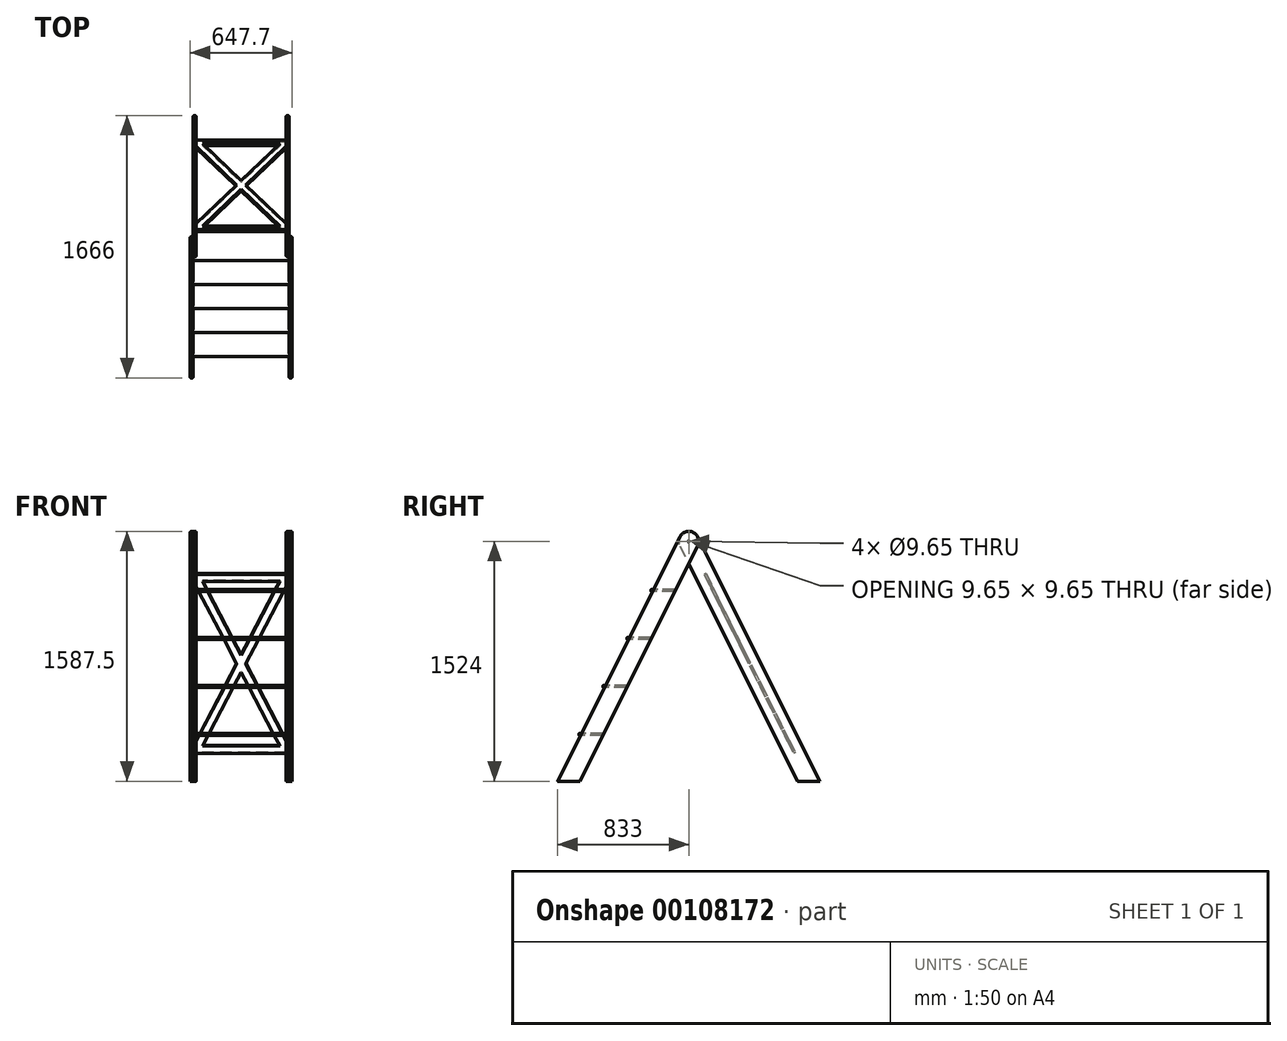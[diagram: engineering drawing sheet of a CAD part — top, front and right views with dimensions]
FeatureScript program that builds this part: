
annotation { "Feature Type Name" : "Feature", "Feature Type Description" : "" }
export const myFeature = defineFeature(function(context is Context, id is Id, definition is map)
    precondition{}
    {
        {
            var Q0;
            Q0=qCreatedBy(makeId("Right.planeOp"),FACE);
            var sketch = newSketch(context, id + "F0", { "sketchPlane" : qUnion([Q0])});
            skLineSegment(sketch, "E0", {"start": v(0, 0) * mm, "end": v(0, 1524) * mm, "construction": true});
            skLineSegment(sketch, "E1.0", {"start": v(-762, 0) * mm, "end": v(-762, 1524) * mm, "construction": true});
            skLineSegment(sketch, "E2", {"start": v(-691, 0) * mm, "end": v(-833, 0) * mm});
            skLineSegment(sketch, "E3.0", {"start": v(0, 304.8) * mm, "end": v(-1233.58, 304.8) * mm, "construction": true});
            skLineSegment(sketch, "E4.0", {"start": v(0, 609.6) * mm, "end": v(-1233.58, 609.6) * mm, "construction": true});
            skLineSegment(sketch, "E5.0", {"start": v(0, 914.4) * mm, "end": v(-1233.58, 914.4) * mm, "construction": true});
            skLineSegment(sketch, "E6.0", {"start": v(0, 1219.2) * mm, "end": v(-1233.58, 1219.2) * mm, "construction": true});
            skArc(sketch, "E7", {"start": v(-28.4, 1467.2) * mm, "mid": v(-14.59, 1462.2) * mm, "end": v(0, 1460.5) * mm, "construction": true});
            skLineSegment(sketch, "E8", {"start": v(0, 1524) * mm, "end": v(-762, 0) * mm, "construction": true});
            skLineSegment(sketch, "E9.0", {"start": v(-56.8, 1552.4) * mm, "end": v(-833, 0) * mm});
            skLineSegment(sketch, "E10.0", {"start": v(56.8, 1495.6) * mm, "end": v(-691, 0) * mm});
            skArc(sketch, "E11.trimOffspring", {"start": v(56.8, 1495.6) * mm, "mid": v(28.4, 1580.8) * mm, "end": v(-56.8, 1552.4) * mm});
            skSolve(sketch);
        }
        {
            var Q0;
            Q0=qSketchRegion(id+"F0",true);
            extrude(context, id + "F1", {"entities" : qUnion([Q0]), "depth" : 19.05 * mm});
        }
        {
            var Q0;
            Q0=makeQuery(id+"F1.opExtrude","CAP_FACE",FACE,{"disambiguationData":[OSD([sQuery(id+"F0.wireOp",EDGE,"E2"),sQuery(id+"F0.wireOp",EDGE,"E9.0"),sQuery(id+"F0.wireOp",EDGE,"E10.0"),sQuery(id+"F0.wireOp",EDGE,"E11.trimOffspring")])],"isStart":true});
            var sketch = newSketch(context, id + "F2", { "sketchPlane" : qUnion([Q0])});
            skLineSegment(sketch, "E12.0", {"start": v(56.8, 1552.4) * mm, "end": v(229.75, 1206.5) * mm});
            skLineSegment(sketch, "E13.0", {"start": v(-56.8, 1495.6) * mm, "end": v(87.75, 1206.5) * mm});
            skLineSegment(sketch, "E14.0", {"start": v(0, 1219.2) * mm, "end": v(1233.58, 1219.2) * mm});
            skLineSegment(sketch, "E15.0", {"start": v(0, 914.4) * mm, "end": v(1233.58, 914.4) * mm});
            skLineSegment(sketch, "E16.0", {"start": v(0, 609.6) * mm, "end": v(1233.58, 609.6) * mm});
            skLineSegment(sketch, "E17.0", {"start": v(0, 304.8) * mm, "end": v(1233.58, 304.8) * mm});
            skLineSegment(sketch, "E18.0", {"start": v(0, 1206.5) * mm, "end": v(1233.58, 1206.5) * mm});
            skLineSegment(sketch, "E19.0", {"start": v(0, 901.7) * mm, "end": v(1233.58, 901.7) * mm});
            skLineSegment(sketch, "E20.0", {"start": v(0, 596.9) * mm, "end": v(1233.58, 596.9) * mm});
            skLineSegment(sketch, "E21.0", {"start": v(0, 292.1) * mm, "end": v(1233.58, 292.1) * mm});
            skLineSegment(sketch, "E22.trimOffspring", {"start": v(375.8, 914.4) * mm, "end": v(382.15, 901.7) * mm});
            skLineSegment(sketch, "E23.trimOffspring", {"start": v(233.8, 914.4) * mm, "end": v(240.15, 901.7) * mm});
            skLineSegment(sketch, "E24.trimOffspring", {"start": v(528.2, 609.6) * mm, "end": v(534.55, 596.9) * mm});
            skLineSegment(sketch, "E25.trimOffspring", {"start": v(386.2, 609.6) * mm, "end": v(392.55, 596.9) * mm});
            skLineSegment(sketch, "E26.trimOffspring", {"start": v(680.6, 304.8) * mm, "end": v(686.95, 292.1) * mm});
            skLineSegment(sketch, "E27.trimOffspring", {"start": v(538.6, 304.8) * mm, "end": v(544.95, 292.1) * mm});
            skPoint(sketch, "E28.orphan", {"position": v(833, 0) * mm});
            skPoint(sketch, "E29.orphan", {"position": v(691, 0) * mm});
            skSolve(sketch);
        }
        {
            var Q0;
            Q0=qSketchRegion(id+"F2",true);
            extrude(context, id + "F3", {"entities" : qUnion([Q0]), "operationType" : NewBodyOperationType.REMOVE, "oppositeDirection" : true, "depth" : 6.35 * mm});
        }
        {
            var Q0;
            Q0=makeQuery(id+"F0.imprint","IMPRINT",FACE,{"disambiguationData":[TD([[makeQuery(id+"F0.imprint","IMPRINT",EDGE,{"derivedFrom":sQuery(id+"F0.wireOp",EDGE,"E2")}),-1.0]])]});
            var sketch = newSketch(context, id + "F4", { "sketchPlane" : qUnion([Q0])});
            skLineSegment(sketch, "E30.0", {"start": v(0, 1524) * mm, "end": v(-762, 0) * mm, "construction": true});
            skPoint(sketch, "E31", {"position": v(0, 1524) * mm});
            skSolve(sketch);
        }
        {
            var Q0;
            Q0=sQuery(id+"F4.wireOp",VERTEX,"E31");
            var Q1;
            Q1=makeQuery(id+"F1.opExtrude","SWEPT_BODY",BODY,{"disambiguationData":[OSD([sQuery(id+"F0.wireOp",EDGE,"E2"),sQuery(id+"F0.wireOp",EDGE,"E9.0"),sQuery(id+"F0.wireOp",EDGE,"E10.0"),sQuery(id+"F0.wireOp",EDGE,"E11.trimOffspring")])]});
            hole(context, id + "F5", {"style" : HoleStyle.SIMPLE, "endStyle" : HoleEndStyle.THROUGH, "oppositeDirection" : true, "holeDiameter" : 9.65 * mm, "locations" : qUnion([Q0]), "scope" : qUnion([Q1]), "isTappedThrough" : true});
        }
        {
            var Q0;
            {var subQ0=sQuery(id+"F0.wireOp",EDGE,"E9.0");Q0=makeQuery(id+"F3.boolean.opBoolean","SPLIT",EDGE,{"disambiguationData":[TD([makeQuery(id+"F3.opExtrude","SWEPT_FACE",FACE,{"disambiguationData":[OSD([sQuery(id+"F2.wireOp",EDGE,"E15.0")])]})])],"derivedFrom":makeQuery(id+"F1.opExtrude","CAP_EDGE",EDGE,{"disambiguationData":[OSD([subQ0])],"isStart":true})});}
            var Q1;
            Q1=makeQuery(id+"F1.opExtrude","CAP_EDGE",EDGE,{"disambiguationData":[OSD([sQuery(id+"F0.wireOp",EDGE,"E9.0")])],"isStart":false});
            var Q2;
            {var subQ0=sQuery(id+"F0.wireOp",EDGE,"E9.0");Q2=makeQuery(id+"F3.boolean.opBoolean","SPLIT",EDGE,{"disambiguationData":[TD([makeQuery(id+"F3.opExtrude","SWEPT_FACE",FACE,{"disambiguationData":[OSD([sQuery(id+"F2.wireOp",EDGE,"E16.0")])]})])],"derivedFrom":makeQuery(id+"F1.opExtrude","CAP_EDGE",EDGE,{"disambiguationData":[OSD([subQ0])],"isStart":true})});}
            var Q3;
            {var subQ0=sQuery(id+"F0.wireOp",EDGE,"E11.trimOffspring");var subQ1=sQuery(id+"F0.wireOp",EDGE,"E9.0");Q3=makeQuery(id+"F3.boolean.opBoolean","SPLIT",EDGE,{"disambiguationData":[TD([makeQuery(id+"F1.opExtrude","SWEPT_FACE",FACE,{"disambiguationData":[OSD([subQ0])]})])],"derivedFrom":makeQuery(id+"F1.opExtrude","CAP_EDGE",EDGE,{"disambiguationData":[OSD([subQ1])],"isStart":true})});}
            var Q4;
            {var subQ0=sQuery(id+"F0.wireOp",EDGE,"E10.0");Q4=makeQuery(id+"F3.boolean.opBoolean","SPLIT",EDGE,{"disambiguationData":[TD([makeQuery(id+"F3.opExtrude","SWEPT_FACE",FACE,{"disambiguationData":[OSD([sQuery(id+"F2.wireOp",EDGE,"E15.0")])]})])],"derivedFrom":makeQuery(id+"F1.opExtrude","CAP_EDGE",EDGE,{"disambiguationData":[OSD([subQ0])],"isStart":true})});}
            var Q5;
            {var subQ0=sQuery(id+"F0.wireOp",EDGE,"E10.0");Q5=makeQuery(id+"F3.boolean.opBoolean","SPLIT",EDGE,{"disambiguationData":[TD([makeQuery(id+"F3.opExtrude","SWEPT_FACE",FACE,{"disambiguationData":[OSD([sQuery(id+"F2.wireOp",EDGE,"E16.0")])]})])],"derivedFrom":makeQuery(id+"F1.opExtrude","CAP_EDGE",EDGE,{"disambiguationData":[OSD([subQ0])],"isStart":true})});}
            var Q6;
            {var subQ0=sQuery(id+"F0.wireOp",EDGE,"E10.0");Q6=makeQuery(id+"F3.boolean.opBoolean","SPLIT",EDGE,{"disambiguationData":[TD([makeQuery(id+"F3.opExtrude","SWEPT_FACE",FACE,{"disambiguationData":[OSD([sQuery(id+"F2.wireOp",EDGE,"E17.0")])]})])],"derivedFrom":makeQuery(id+"F1.opExtrude","CAP_EDGE",EDGE,{"disambiguationData":[OSD([subQ0])],"isStart":true})});}
            var Q7;
            {var subQ0=sQuery(id+"F0.wireOp",EDGE,"E9.0");Q7=makeQuery(id+"F3.boolean.opBoolean","SPLIT",EDGE,{"disambiguationData":[TD([makeQuery(id+"F3.opExtrude","SWEPT_FACE",FACE,{"disambiguationData":[OSD([sQuery(id+"F2.wireOp",EDGE,"E17.0")])]})])],"derivedFrom":makeQuery(id+"F1.opExtrude","CAP_EDGE",EDGE,{"disambiguationData":[OSD([subQ0])],"isStart":true})});}
            var Q8;
            {var subQ0=sQuery(id+"F0.wireOp",EDGE,"E2");var subQ1=sQuery(id+"F0.wireOp",EDGE,"E9.0");Q8=makeQuery(id+"F3.boolean.opBoolean","SPLIT",EDGE,{"disambiguationData":[TD([makeQuery(id+"F1.opExtrude","SWEPT_FACE",FACE,{"disambiguationData":[OSD([subQ0])]})])],"derivedFrom":makeQuery(id+"F1.opExtrude","CAP_EDGE",EDGE,{"disambiguationData":[OSD([subQ1])],"isStart":true})});}
            var Q9;
            {var subQ0=sQuery(id+"F0.wireOp",EDGE,"E2");var subQ1=sQuery(id+"F0.wireOp",EDGE,"E10.0");Q9=makeQuery(id+"F3.boolean.opBoolean","SPLIT",EDGE,{"disambiguationData":[TD([makeQuery(id+"F1.opExtrude","SWEPT_FACE",FACE,{"disambiguationData":[OSD([subQ0])]})])],"derivedFrom":makeQuery(id+"F1.opExtrude","CAP_EDGE",EDGE,{"disambiguationData":[OSD([subQ1])],"isStart":true})});}
            fillet(context, id + "F6", {"entities" : qUnion([Q0, Q1, Q2, Q3, Q4, Q5, Q6, Q7, Q8, Q9]), "radius" : 6.35 * mm, "tangentPropagation" : true, "allowEdgeOverflow" : false});
        }
        {
            var Q0;
            Q0=makeQuery(id+"F0.imprint","IMPRINT",FACE,{"disambiguationData":[TD([[makeQuery(id+"F0.imprint","IMPRINT",EDGE,{"derivedFrom":sQuery(id+"F0.wireOp",EDGE,"E2")}),-1.0]])]});
            var sketch = newSketch(context, id + "F7", { "sketchPlane" : qUnion([Q0])});
            skLineSegment(sketch, "E32.0", {"start": v(0, 0) * mm, "end": v(0, 1524) * mm});
            skLineSegment(sketch, "E33.0", {"start": v(-762, 0) * mm, "end": v(-762, 1524) * mm, "construction": true});
            skLineSegment(sketch, "E34.0", {"start": v(-56.8, 1552.4) * mm, "end": v(-833, 0) * mm, "construction": true});
            skArc(sketch, "E35.0", {"start": v(56.8, 1495.6) * mm, "mid": v(28.4, 1580.8) * mm, "end": v(-56.8, 1552.4) * mm, "construction": true});
            skLineSegment(sketch, "E36.0", {"start": v(56.8, 1495.6) * mm, "end": v(-691, 0) * mm, "construction": true});
            skLineSegment(sketch, "E37.0", {"start": v(-691, 0) * mm, "end": v(-833, 0) * mm, "construction": true});
            skArc(sketch, "E38.MirrorCS", {"start": v(-56.8, 1495.6) * mm, "mid": v(-28.4, 1580.8) * mm, "end": v(56.8, 1552.4) * mm});
            skLineSegment(sketch, "E39.MirrorCS", {"start": v(56.8, 1552.4) * mm, "end": v(833, 0) * mm});
            skLineSegment(sketch, "E40.MirrorCS", {"start": v(691, 0) * mm, "end": v(833, 0) * mm});
            skLineSegment(sketch, "E41.MirrorCS", {"start": v(-56.8, 1495.6) * mm, "end": v(691, 0) * mm});
            skCircle(sketch, "E42.0", {"center": v(0, 1524) * mm, "radius": 4.83 * mm});
            skSolve(sketch);
        }
        {
            var Q0;
            Q0=qSketchRegion(id+"F7",true);
            extrude(context, id + "F8", {"entities" : qUnion([Q0]), "oppositeDirection" : true, "depth" : 19.05 * mm});
        }
        {
            var Q0;
            Q0=makeQuery(id+"F8.opExtrude","CAP_EDGE",EDGE,{"disambiguationData":[OSD([sQuery(id+"F7.wireOp",EDGE,"E39.MirrorCS")])],"isStart":false});
            var Q1;
            Q1=makeQuery(id+"F8.opExtrude","CAP_EDGE",EDGE,{"disambiguationData":[OSD([sQuery(id+"F7.wireOp",EDGE,"E38.MirrorCS")])],"isStart":false});
            var Q2;
            Q2=makeQuery(id+"F8.opExtrude","CAP_EDGE",EDGE,{"disambiguationData":[OSD([sQuery(id+"F7.wireOp",EDGE,"E41.MirrorCS")])],"isStart":false});
            var Q3;
            Q3=makeQuery(id+"F8.opExtrude","CAP_EDGE",EDGE,{"disambiguationData":[OSD([sQuery(id+"F7.wireOp",EDGE,"E41.MirrorCS")])],"isStart":true});
            var Q4;
            Q4=makeQuery(id+"F8.opExtrude","CAP_EDGE",EDGE,{"disambiguationData":[OSD([sQuery(id+"F7.wireOp",EDGE,"E38.MirrorCS")])],"isStart":true});
            var Q5;
            Q5=makeQuery(id+"F8.opExtrude","CAP_EDGE",EDGE,{"disambiguationData":[OSD([sQuery(id+"F7.wireOp",EDGE,"E39.MirrorCS")])],"isStart":true});
            fillet(context, id + "F9", {"entities" : qUnion([Q0, Q1, Q2, Q3, Q4, Q5]), "radius" : 6.35 * mm, "tangentPropagation" : true, "allowEdgeOverflow" : false});
        }
        {
            var Q0;
            Q0=makeQuery(id+"F8.opExtrude","SWEPT_FACE",FACE,{"disambiguationData":[OSD([sQuery(id+"F7.wireOp",EDGE,"E39.MirrorCS")])]});
            cPlane(context, id + "F10", {"entities" : qUnion([Q0]), "cplaneType" : CPlaneType.OFFSET, "offset" : 63.5 * mm, "oppositeDirection" : true, "width" : 152.4 * mm, "height" : 152.4 * mm});
        }
        {
            var Q0;
            Q0=makeQuery(id+"F0.imprint","IMPRINT",FACE,{"disambiguationData":[TD([[makeQuery(id+"F0.imprint","IMPRINT",EDGE,{"derivedFrom":sQuery(id+"F0.wireOp",EDGE,"E2")}),-1.0]])]});
            cPlane(context, id + "F11", {"entities" : qUnion([Q0]), "cplaneType" : CPlaneType.OFFSET, "offset" : 304.8 * mm, "oppositeDirection" : true, "width" : 152.4 * mm, "height" : 152.4 * mm});
        }
        {
            var Q0;
            Q0=makeQuery(id+"F1.opExtrude","SWEPT_BODY",BODY,{"disambiguationData":[OSD([sQuery(id+"F0.wireOp",EDGE,"E2"),sQuery(id+"F0.wireOp",EDGE,"E9.0"),sQuery(id+"F0.wireOp",EDGE,"E10.0"),sQuery(id+"F0.wireOp",EDGE,"E11.trimOffspring")])]});
            var Q1;
            Q1=makeQuery(id+"F8.opExtrude","SWEPT_BODY",BODY,{"disambiguationData":[OSD([sQuery(id+"F7.wireOp",EDGE,"E38.MirrorCS"),sQuery(id+"F7.wireOp",EDGE,"E39.MirrorCS"),sQuery(id+"F7.wireOp",EDGE,"E40.MirrorCS"),sQuery(id+"F7.wireOp",EDGE,"E41.MirrorCS"),sQuery(id+"F7.wireOp",EDGE,"E42.0")])]});
            var Q2;
            Q2=qCreatedBy(id+"F11.planeOp",FACE);
            mirror(context, id + "F12", {"entities" : qUnion([Q0, Q1]), "mirrorPlane" : qUnion([Q2])});
        }
        {
            var Q0;
            Q0=qCreatedBy(id+"F10.planeOp",FACE);
            var sketch = newSketch(context, id + "F13", { "sketchPlane" : qUnion([Q0])});
            skLineSegment(sketch, "E43.0", {"start": v(19.05, 1131.88) * mm, "end": v(19.05, 1046.63) * mm});
            skLineSegment(sketch, "E44.0", {"start": v(590.55, 1131.88) * mm, "end": v(590.55, 1046.63) * mm});
            skLineSegment(sketch, "E45", {"start": v(19.05, 496.88) * mm, "end": v(590.55, 496.88) * mm, "construction": true});
            skLineSegment(sketch, "E46.0", {"start": v(19.05, 1106.48) * mm, "end": v(590.55, 1106.48) * mm, "construction": true});
            skLineSegment(sketch, "E47.MirrorCS", {"start": v(19.05, -112.72) * mm, "end": v(590.55, -112.72) * mm, "construction": true});
            skLineSegment(sketch, "E48", {"start": v(590.55, -112.72) * mm, "end": v(19.05, 1106.48) * mm, "construction": true});
            skLineSegment(sketch, "E49.0", {"start": v(590.55, -52.88) * mm, "end": v(42.05, 1117.26) * mm});
            skLineSegment(sketch, "E50.MirrorCS", {"start": v(633.32, -263.8) * mm, "end": v(562.5, -112.72) * mm});
            skLineSegment(sketch, "E51.0", {"start": v(19.05, 1131.88) * mm, "end": v(590.55, 1131.88) * mm});
            skLineSegment(sketch, "E52.MirrorCS", {"start": v(19.05, 1081.08) * mm, "end": v(550.6, 1081.08) * mm});
            skLineSegment(sketch, "E53", {"start": v(304.8, 496.88) * mm, "end": v(304.8, -558.13) * mm, "construction": true});
            skLineSegment(sketch, "E54.MirrorCS", {"start": v(19.05, -87.32) * mm, "end": v(590.55, -87.32) * mm});
            skLineSegment(sketch, "E55.MirrorCS", {"start": v(19.05, -138.12) * mm, "end": v(590.55, -138.12) * mm});
            skLineSegment(sketch, "E56.MirrorCS", {"start": v(-23.72, -263.8) * mm, "end": v(47.1, -112.72) * mm});
            skLineSegment(sketch, "E57.MirrorCS", {"start": v(19.05, -52.88) * mm, "end": v(550.6, 1081.08) * mm});
            skPoint(sketch, "E58.orphan", {"position": v(-69.71, -242.24) * mm});
            skPoint(sketch, "E59.orphan", {"position": v(19.05, -369.35) * mm});
            skLineSegment(sketch, "E60.trimOffspring", {"start": v(19.05, -52.88) * mm, "end": v(19.05, -138.12) * mm});
            skLineSegment(sketch, "E61.trimOffspring", {"start": v(59, -87.32) * mm, "end": v(613.55, 1095.7) * mm});
            skLineSegment(sketch, "E62.trimOffspring", {"start": v(550.6, -87.32) * mm, "end": v(19.05, 1046.63) * mm});
            skPoint(sketch, "E63.orphan", {"position": v(679.31, -242.24) * mm});
            skLineSegment(sketch, "E64.trimOffspring", {"start": v(590.55, -52.88) * mm, "end": v(590.55, -138.12) * mm});
            skPoint(sketch, "E65.orphan", {"position": v(590.55, -369.35) * mm});
            skLineSegment(sketch, "E66.trimOffspring", {"start": v(562.5, 1106.48) * mm, "end": v(567.55, 1117.26) * mm});
            skPoint(sketch, "E67.orphan", {"position": v(590.55, 1081.08) * mm});
            skPoint(sketch, "E68.orphan", {"position": v(19.05, 1363.1) * mm});
            skPoint(sketch, "E69.orphan", {"position": v(-3.95, 1095.7) * mm});
            skPoint(sketch, "E70.orphan", {"position": v(590.55, 1363.1) * mm});
            skSolve(sketch);
        }
        {
            var Q0;
            Q0=qSketchRegion(id+"F13",true);
            extrude(context, id + "F14", {"entities" : qUnion([Q0]), "endBound" : BoundingType.SYMMETRIC, "depth" : 12.7 * mm});
        }
        {
            var Q0;
            Q0=makeQuery(id+"F3.boolean.opBoolean","COPY",FACE,{"derivedFrom":makeQuery(id+"F3.opExtrude","CAP_FACE",FACE,{"disambiguationData":[OSD([sQuery(id+"F2.wireOp",EDGE,"E17.0"),sQuery(id+"F2.wireOp",EDGE,"E21.0"),sQuery(id+"F2.wireOp",EDGE,"E26.trimOffspring"),sQuery(id+"F2.wireOp",EDGE,"E27.trimOffspring")])],"isStart":false})});
            var sketch = newSketch(context, id + "F15", { "sketchPlane" : qUnion([Q0])});
            skLineSegment(sketch, "E71.0", {"start": v(552.05, 292.1) * mm, "end": v(697.35, 292.1) * mm});
            skLineSegment(sketch, "E72.0", {"start": v(538.6, 304.8) * mm, "end": v(697.35, 304.8) * mm});
            skLineSegment(sketch, "E73.0", {"start": v(-56.8, 1495.6) * mm, "end": v(691, 0) * mm, "construction": true});
            skLineSegment(sketch, "E74", {"start": v(552.05, 292.1) * mm, "end": v(544.95, 292.1) * mm});
            skLineSegment(sketch, "E75", {"start": v(544.95, 292.1) * mm, "end": v(544.95, 304.8) * mm});
            skLineSegment(sketch, "E76.0", {"start": v(697.35, 292.1) * mm, "end": v(697.35, 304.8) * mm});
            skPoint(sketch, "E77.orphan", {"position": v(680.6, 304.8) * mm});
            skPoint(sketch, "E78.orphan", {"position": v(679.85, 292.1) * mm});
            skLineSegment(sketch, "E79.0", {"start": v(311.8, 596.9) * mm, "end": v(544.95, 596.9) * mm});
            skLineSegment(sketch, "E80.0", {"start": v(298.35, 609.6) * mm, "end": v(544.95, 609.6) * mm});
            skLineSegment(sketch, "E81", {"start": v(392.55, 596.9) * mm, "end": v(311.8, 596.9) * mm});
            skLineSegment(sketch, "E82", {"start": v(392.55, 596.9) * mm, "end": v(392.55, 609.6) * mm});
            skLineSegment(sketch, "E83.0", {"start": v(544.95, 596.9) * mm, "end": v(544.95, 609.6) * mm});
            skPoint(sketch, "E84.orphan", {"position": v(528.2, 609.6) * mm});
            skPoint(sketch, "E85.orphan", {"position": v(527.45, 596.9) * mm});
            skLineSegment(sketch, "E86.1", {"start": v(392.55, 596.9) * mm, "end": v(399.65, 596.9) * mm});
            skLineSegment(sketch, "E87.0", {"start": v(240.15, 901.7) * mm, "end": v(247.25, 901.7) * mm});
            skLineSegment(sketch, "E88.0", {"start": v(247.25, 901.7) * mm, "end": v(392.55, 901.7) * mm});
            skLineSegment(sketch, "E89.0", {"start": v(233.8, 914.4) * mm, "end": v(392.55, 914.4) * mm});
            skLineSegment(sketch, "E90", {"start": v(247.25, 901.7) * mm, "end": v(240.15, 901.7) * mm});
            skLineSegment(sketch, "E91", {"start": v(240.15, 901.7) * mm, "end": v(240.15, 914.4) * mm});
            skLineSegment(sketch, "E92.0", {"start": v(392.55, 901.7) * mm, "end": v(392.55, 914.4) * mm});
            skPoint(sketch, "E93.orphan", {"position": v(375.8, 914.4) * mm});
            skPoint(sketch, "E94.orphan", {"position": v(375.05, 901.7) * mm});
            skLineSegment(sketch, "E95.0", {"start": v(87.75, 1206.5) * mm, "end": v(94.85, 1206.5) * mm});
            skLineSegment(sketch, "E96.0", {"start": v(94.85, 1206.5) * mm, "end": v(240.15, 1206.5) * mm});
            skLineSegment(sketch, "E97.0", {"start": v(81.4, 1219.2) * mm, "end": v(240.15, 1219.2) * mm});
            skLineSegment(sketch, "E98", {"start": v(94.85, 1206.5) * mm, "end": v(87.75, 1206.5) * mm});
            skLineSegment(sketch, "E99", {"start": v(87.75, 1206.5) * mm, "end": v(87.75, 1219.2) * mm});
            skLineSegment(sketch, "E100.0", {"start": v(240.15, 1206.5) * mm, "end": v(240.15, 1219.2) * mm});
            skPoint(sketch, "E101.orphan", {"position": v(223.4, 1219.2) * mm});
            skPoint(sketch, "E102.orphan", {"position": v(222.65, 1206.5) * mm});
            skSolve(sketch);
        }
        {
            var Q0;
            Q0=qSketchRegion(id+"F15",true);
            extrude(context, id + "F16", {"entities" : qUnion([Q0]), "depth" : 622.3 * mm});
        }
        {
            var Q0;
            Q0=makeQuery(id+"F16.opExtrude","CAP_EDGE",EDGE,{"disambiguationData":[OSD([sQuery(id+"F15.wireOp",EDGE,"E76.0")])],"isStart":true});
            var Q1;
            Q1=makeQuery(id+"F16.opExtrude","CAP_EDGE",EDGE,{"disambiguationData":[OSD([sQuery(id+"F15.wireOp",EDGE,"E83.0")])],"isStart":true});
            var Q2;
            Q2=makeQuery(id+"F16.opExtrude","CAP_EDGE",EDGE,{"disambiguationData":[OSD([sQuery(id+"F15.wireOp",EDGE,"E92.0")])],"isStart":true});
            var Q3;
            Q3=makeQuery(id+"F16.opExtrude","CAP_EDGE",EDGE,{"disambiguationData":[OSD([sQuery(id+"F15.wireOp",EDGE,"E100.0")])],"isStart":true});
            var Q4;
            Q4=makeQuery(id+"F16.opExtrude","CAP_EDGE",EDGE,{"disambiguationData":[OSD([sQuery(id+"F15.wireOp",EDGE,"E100.0")])],"isStart":false});
            var Q5;
            Q5=makeQuery(id+"F16.opExtrude","CAP_EDGE",EDGE,{"disambiguationData":[OSD([sQuery(id+"F15.wireOp",EDGE,"E92.0")])],"isStart":false});
            var Q6;
            Q6=makeQuery(id+"F16.opExtrude","CAP_EDGE",EDGE,{"disambiguationData":[OSD([sQuery(id+"F15.wireOp",EDGE,"E83.0")])],"isStart":false});
            var Q7;
            Q7=makeQuery(id+"F16.opExtrude","CAP_EDGE",EDGE,{"disambiguationData":[OSD([sQuery(id+"F15.wireOp",EDGE,"E76.0")])],"isStart":false});
            chamfer(context, id + "F17", {"entities" : qUnion([Q0, Q1, Q2, Q3, Q4, Q5, Q6, Q7]), "width" : 12.7 * mm, "tangentPropagation" : true});
        }
        {
            var Q0;
            Q0=makeQuery(id+"F16.opExtrude","SWEPT_EDGE",EDGE,{"disambiguationData":[OSD([sQuery(id+"F15.wireOp",EDGE,"E97.0"),sQuery(id+"F15.wireOp",EDGE,"E100.0")])]});
            var Q1;
            Q1=makeQuery(id+"F16.opExtrude","SWEPT_EDGE",EDGE,{"disambiguationData":[OSD([sQuery(id+"F15.wireOp",EDGE,"E96.0"),sQuery(id+"F15.wireOp",EDGE,"E100.0")])]});
            var Q2;
            Q2=makeQuery(id+"F16.opExtrude","SWEPT_EDGE",EDGE,{"disambiguationData":[OSD([sQuery(id+"F15.wireOp",EDGE,"E89.0"),sQuery(id+"F15.wireOp",EDGE,"E92.0")])]});
            var Q3;
            Q3=makeQuery(id+"F16.opExtrude","SWEPT_EDGE",EDGE,{"disambiguationData":[OSD([sQuery(id+"F15.wireOp",EDGE,"E88.0"),sQuery(id+"F15.wireOp",EDGE,"E92.0")])]});
            var Q4;
            Q4=makeQuery(id+"F16.opExtrude","SWEPT_EDGE",EDGE,{"disambiguationData":[OSD([sQuery(id+"F15.wireOp",EDGE,"E80.0"),sQuery(id+"F15.wireOp",EDGE,"E83.0")])]});
            var Q5;
            Q5=makeQuery(id+"F16.opExtrude","SWEPT_EDGE",EDGE,{"disambiguationData":[OSD([sQuery(id+"F15.wireOp",EDGE,"E79.0"),sQuery(id+"F15.wireOp",EDGE,"E83.0")])]});
            var Q6;
            Q6=makeQuery(id+"F16.opExtrude","SWEPT_EDGE",EDGE,{"disambiguationData":[OSD([sQuery(id+"F15.wireOp",EDGE,"E97.0"),sQuery(id+"F15.wireOp",EDGE,"E99")])]});
            var Q7;
            Q7=makeQuery(id+"F16.opExtrude","SWEPT_EDGE",EDGE,{"disambiguationData":[OSD([sQuery(id+"F15.wireOp",EDGE,"E98"),sQuery(id+"F15.wireOp",EDGE,"E99")])]});
            var Q8;
            Q8=makeQuery(id+"F16.opExtrude","SWEPT_EDGE",EDGE,{"disambiguationData":[OSD([sQuery(id+"F15.wireOp",EDGE,"E89.0"),sQuery(id+"F15.wireOp",EDGE,"E91")])]});
            var Q9;
            Q9=makeQuery(id+"F16.opExtrude","SWEPT_EDGE",EDGE,{"disambiguationData":[OSD([sQuery(id+"F15.wireOp",EDGE,"E90"),sQuery(id+"F15.wireOp",EDGE,"E91")])]});
            var Q10;
            Q10=makeQuery(id+"F16.opExtrude","SWEPT_EDGE",EDGE,{"disambiguationData":[OSD([sQuery(id+"F15.wireOp",EDGE,"E80.0"),sQuery(id+"F15.wireOp",EDGE,"E82")])]});
            var Q11;
            Q11=makeQuery(id+"F16.opExtrude","SWEPT_EDGE",EDGE,{"disambiguationData":[OSD([sQuery(id+"F15.wireOp",EDGE,"E82"),sQuery(id+"F15.wireOp",EDGE,"E86.1")])]});
            var Q12;
            Q12=makeQuery(id+"F16.opExtrude","SWEPT_EDGE",EDGE,{"disambiguationData":[OSD([sQuery(id+"F15.wireOp",EDGE,"E72.0"),sQuery(id+"F15.wireOp",EDGE,"E75")])]});
            var Q13;
            Q13=makeQuery(id+"F16.opExtrude","SWEPT_EDGE",EDGE,{"disambiguationData":[OSD([sQuery(id+"F2.wireOp",EDGE,"E27.trimOffspring"),sQuery(id+"F15.wireOp",EDGE,"E74"),sQuery(id+"F15.wireOp",EDGE,"E75")])]});
            var Q14;
            Q14=makeQuery(id+"F16.opExtrude","SWEPT_EDGE",EDGE,{"disambiguationData":[OSD([sQuery(id+"F15.wireOp",EDGE,"E72.0"),sQuery(id+"F15.wireOp",EDGE,"E76.0")])]});
            var Q15;
            Q15=makeQuery(id+"F16.opExtrude","SWEPT_EDGE",EDGE,{"disambiguationData":[OSD([sQuery(id+"F15.wireOp",EDGE,"E71.0"),sQuery(id+"F15.wireOp",EDGE,"E76.0")])]});
            fillet(context, id + "F18", {"entities" : qUnion([Q0, Q1, Q2, Q3, Q4, Q5, Q6, Q7, Q8, Q9, Q10, Q11, Q12, Q13, Q14, Q15]), "radius" : 3.17 * mm, "tangentPropagation" : true, "allowEdgeOverflow" : false});
        }
    });
